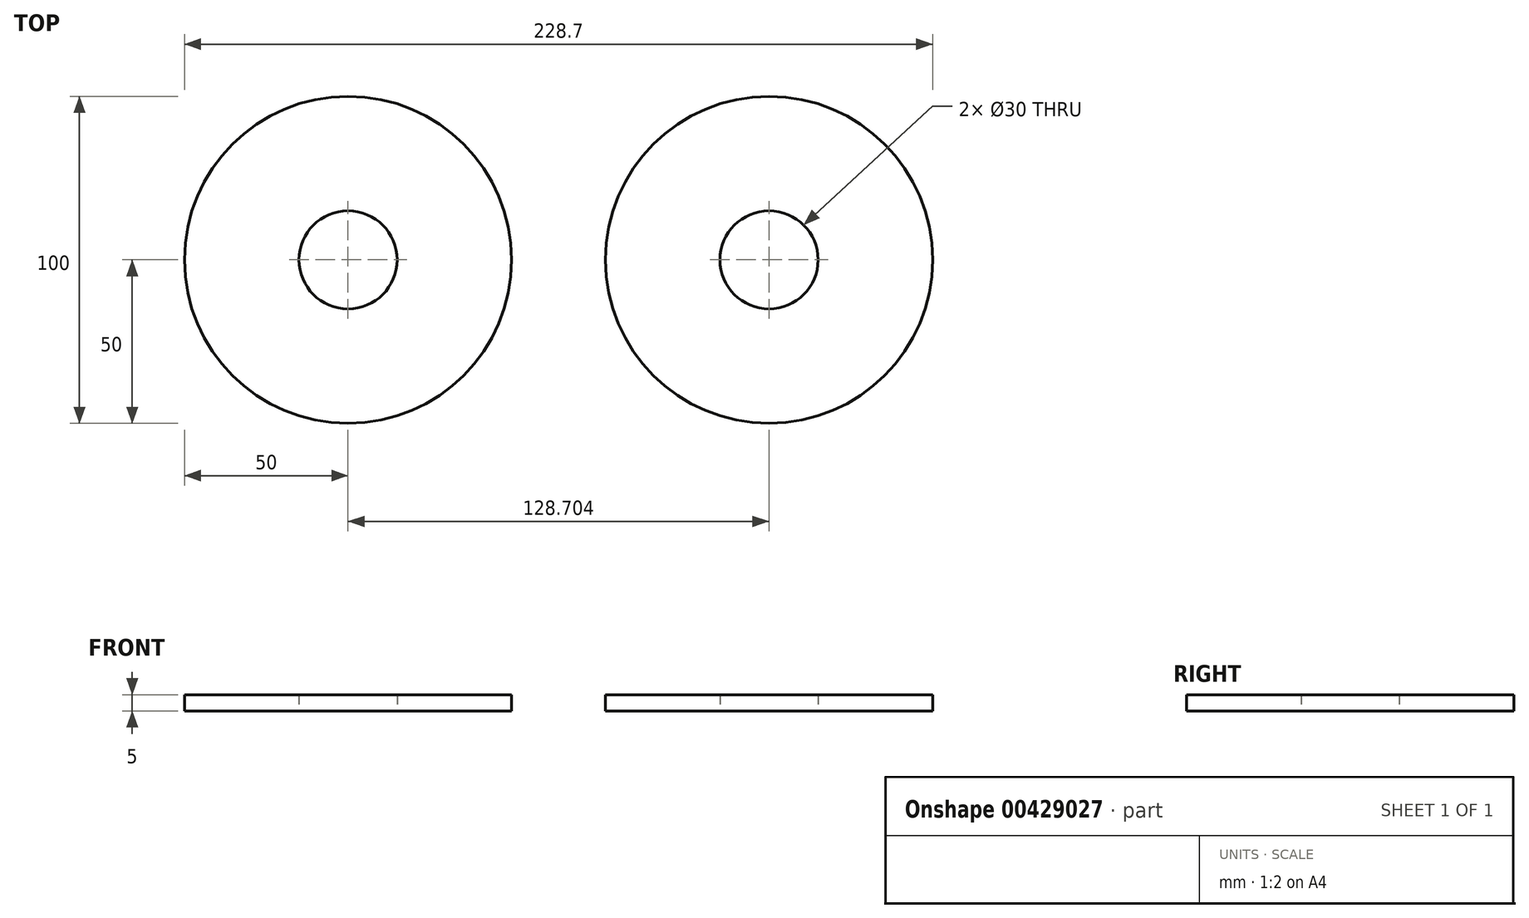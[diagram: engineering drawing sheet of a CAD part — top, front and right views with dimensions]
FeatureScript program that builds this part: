
annotation { "Feature Type Name" : "Feature", "Feature Type Description" : "" }
export const myFeature = defineFeature(function(context is Context, id is Id, definition is map)
    precondition{}
    {
        {
            var Q0;
            Q0=qCreatedBy(makeId("Top.planeOp"),FACE);
            var sketch = newSketch(context, id + "F0", { "sketchPlane" : qUnion([Q0])});
            skCircle(sketch, "E0", {"center": v(0, 0) * mm, "radius": 50 * mm});
            skCircle(sketch, "E1.MirrorC", {"center": v(128.7, 0) * mm, "radius": 50 * mm});
            skCircle(sketch, "E2", {"center": v(0, 0) * mm, "radius": 15 * mm});
            skCircle(sketch, "E3", {"center": v(128.7, 0) * mm, "radius": 15 * mm});
            skSolve(sketch);
        }
        {
            var Q0;
            Q0 = qSketchRegion(id + "F0", true);
            extrude(context, id + "F1", {"entities" : qUnion([Q0]), "depth" : 5 * mm});
        }
    });
